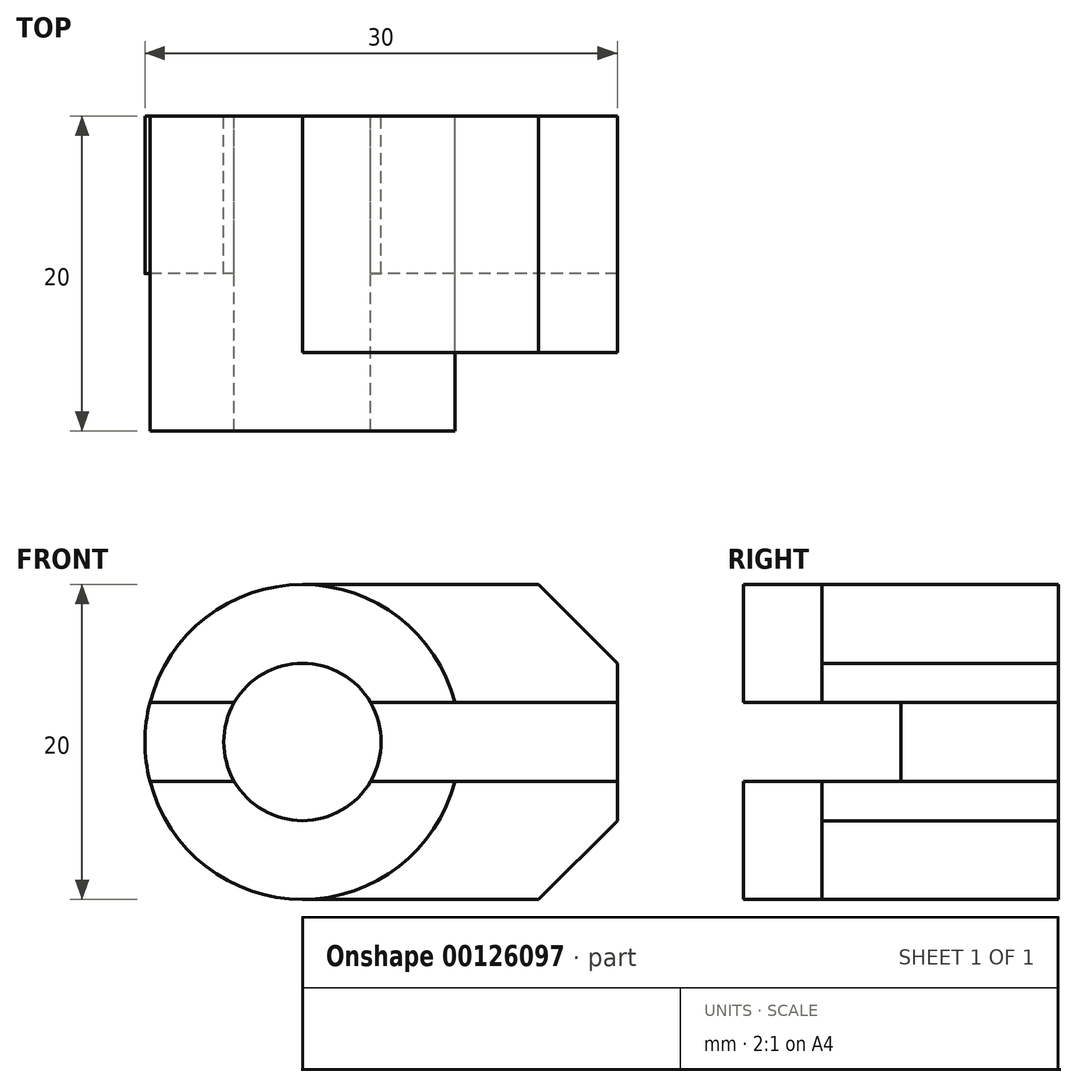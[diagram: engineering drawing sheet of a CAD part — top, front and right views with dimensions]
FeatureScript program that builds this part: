
annotation { "Feature Type Name" : "Feature", "Feature Type Description" : "" }
export const myFeature = defineFeature(function(context is Context, id is Id, definition is map)
    precondition{}
    {
        {
            var Q0;
            Q0=qCreatedBy(makeId("Front.planeOp"),FACE);
            var sketch = newSketch(context, id + "F0", { "sketchPlane" : qUnion([Q0])});
            skCircle(sketch, "E0", {"center": v(0, 0) * mm, "radius": 5 * mm});
            skLineSegment(sketch, "E1", {"start": v(15, 10) * mm, "end": v(20, 5) * mm});
            skLineSegment(sketch, "E2", {"start": v(20, 5) * mm, "end": v(20, 2.5) * mm});
            skLineSegment(sketch, "E3", {"start": v(20, 2.5) * mm, "end": v(4.33, 2.5) * mm});
            skLineSegment(sketch, "E4", {"start": v(20, 2.5) * mm, "end": v(20, -2.5) * mm});
            skLineSegment(sketch, "E5", {"start": v(20, -2.5) * mm, "end": v(4.33, -2.5) * mm});
            skLineSegment(sketch, "E6", {"start": v(20, -2.5) * mm, "end": v(20, -5) * mm});
            skLineSegment(sketch, "E7", {"start": v(20, -5) * mm, "end": v(15, -10) * mm});
            skLineSegment(sketch, "E8", {"start": v(-4.33, 2.5) * mm, "end": v(-9.68, 2.5) * mm});
            skLineSegment(sketch, "E9", {"start": v(-4.33, -2.5) * mm, "end": v(-9.68, -2.5) * mm});
            skArc(sketch, "E10", {"start": v(9.68, 2.5) * mm, "mid": v(0, 10) * mm, "end": v(-9.68, 2.5) * mm});
            skArc(sketch, "E11", {"start": v(-9.68, -2.5) * mm, "mid": v(0, -10) * mm, "end": v(9.68, -2.5) * mm});
            skArc(sketch, "E12", {"start": v(-9.68, 2.5) * mm, "mid": v(-10, 0) * mm, "end": v(-9.68, -2.5) * mm});
            skLineSegment(sketch, "E13", {"start": v(0, 10) * mm, "end": v(15, 10) * mm});
            skLineSegment(sketch, "E14", {"start": v(15, -10) * mm, "end": v(0, -10) * mm});
            skPoint(sketch, "E14.endSnap0", {"position": v(0, -10) * mm});
            skSolve(sketch);
        }
        {
            var Q0;
            Q0=makeQuery(id+"F0.imprint","IMPRINT",FACE,{"disambiguationData":[TD([[makeQuery(id+"F0.imprint","IMPRINT",EDGE,{"derivedFrom":sQuery(id+"F0.wireOp",EDGE,"E1")}),-1.0]])]});
            var Q1;
            {var subQ4=sQuery(id+"F0.wireOp",EDGE,"E6");Q1=makeQuery(id+"F0.imprint","IMPRINT",FACE,{"disambiguationData":[TD([[makeQuery(id+"F0.imprint","IMPRINT",EDGE,{"derivedFrom":subQ4}),-1.0]])]});}
            extrude(context, id + "F1", {"entities" : qUnion([Q0, Q1]), "depth" : 15 * mm});
        }
        {
            var Q0;
            {var subQ4=sQuery(id+"F0.wireOp",EDGE,"E8");Q0=makeQuery(id+"F0.imprint","IMPRINT",FACE,{"disambiguationData":[TD([[makeQuery(id+"F0.imprint","IMPRINT",EDGE,{"derivedFrom":subQ4}),-1.0]])]});}
            var Q1;
            {var subQ0=sQuery(id+"F0.wireOp",EDGE,"E9");Q1=makeQuery(id+"F0.imprint","IMPRINT",FACE,{"disambiguationData":[TD([[makeQuery(id+"F0.imprint","IMPRINT",EDGE,{"derivedFrom":subQ0}),1.0]])]});}
            extrude(context, id + "F2", {"entities" : qUnion([Q0, Q1]), "depth" : 20 * mm});
        }
        {
            var Q0;
            {var subQ0=sQuery(id+"F0.wireOp",EDGE,"E4");Q0=makeQuery(id+"F0.imprint","IMPRINT",FACE,{"disambiguationData":[TD([[makeQuery(id+"F0.imprint","IMPRINT",EDGE,{"derivedFrom":subQ0}),-1.0]])]});}
            var Q1;
            {var subQ0=sQuery(id+"F0.wireOp",EDGE,"E8");Q1=makeQuery(id+"F0.imprint","IMPRINT",FACE,{"disambiguationData":[TD([[makeQuery(id+"F0.imprint","IMPRINT",EDGE,{"derivedFrom":subQ0}),1.0]])]});}
            extrude(context, id + "F3", {"entities" : qUnion([Q0, Q1]), "depth" : 10 * mm});
        }
    });
